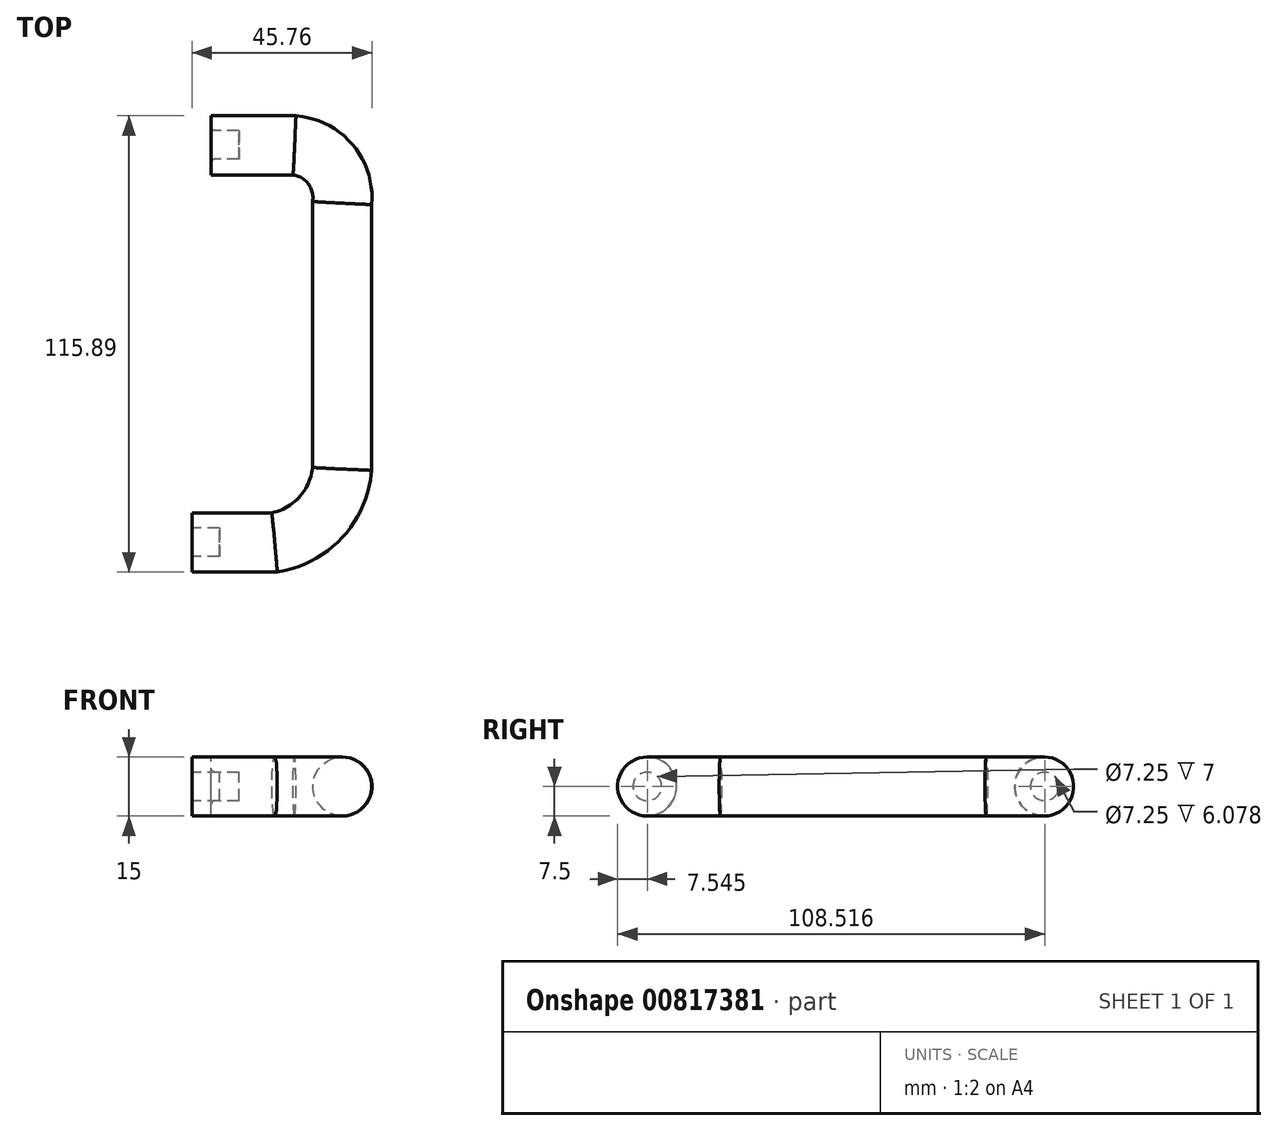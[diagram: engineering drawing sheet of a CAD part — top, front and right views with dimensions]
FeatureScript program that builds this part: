
annotation { "Feature Type Name" : "Feature", "Feature Type Description" : "" }
export const myFeature = defineFeature(function(context is Context, id is Id, definition is map)
    precondition{}
    {
        {
            var Q0;
            Q0=qCreatedBy(makeId("Right.planeOp"),FACE);
            cPlane(context, id + "F0", {"entities" : qUnion([Q0]), "cplaneType" : CPlaneType.OFFSET, "offset" : 5 * mm, "width" : 150 * mm, "height" : 150 * mm});
        }
        {
            var Q0;
            Q0=qCreatedBy(id+"F0.planeOp",FACE);
            var sketch = newSketch(context, id + "F1", { "sketchPlane" : qUnion([Q0])});
            skCircle(sketch, "E0", {"center": v(50.25, 0) * mm, "radius": 7.5 * mm});
            skSolve(sketch);
        }
        {
            var Q0;
            Q0=qCreatedBy(makeId("Top.planeOp"),FACE);
            var sketch = newSketch(context, id + "F2", { "sketchPlane" : qUnion([Q0])});
            skLineSegment(sketch, "E1", {"start": v(0, -50.66) * mm, "end": v(21.06, -50.66) * mm});
            skLineSegment(sketch, "E2", {"start": v(38.2, -32) * mm, "end": v(38.2, 35.56) * mm});
            skLineSegment(sketch, "E3", {"start": v(26.12, 50.27) * mm, "end": v(4.92, 50.27) * mm});
            skArc(sketch, "E4", {"start": v(38.2, 35.56) * mm, "mid": v(35.25, 45.46) * mm, "end": v(26.12, 50.27) * mm});
            skArc(sketch, "E5", {"start": v(21.06, -50.66) * mm, "mid": v(32.79, -44.23) * mm, "end": v(38.2, -32) * mm});
            skSolve(sketch);
        }
        {
            var Q0;
            Q0=makeQuery(id+"F1.imprint","IMPRINT",FACE,{"disambiguationData":[TD([[makeQuery(id+"F1.imprint","IMPRINT",EDGE,{"derivedFrom":sQuery(id+"F1.wireOp",EDGE,"E0")}),1.0]])]});
            var Q1;
            Q1=sQuery(id+"F2.wireOp",EDGE,"E3");
            var Q2;
            Q2=sQuery(id+"F2.wireOp",EDGE,"E2");
            var Q3;
            Q3=sQuery(id+"F2.wireOp",EDGE,"E1");
            var Q4;
            Q4=sQuery(id+"F2.wireOp",EDGE,"E4");
            var Q5;
            Q5=sQuery(id+"F2.wireOp",EDGE,"E5");
            sweep(context, id + "F3", {"profiles" : qUnion([Q0]), "path" : qUnion([Q1, Q2, Q3, Q4, Q5])});
        }
        {
            var Q0;
            Q0=qCreatedBy(makeId("Right.planeOp"),FACE);
            var sketch = newSketch(context, id + "F4", { "sketchPlane" : qUnion([Q0])});
            skCircle(sketch, "E6", {"center": v(-50.6, 0) * mm, "radius": 3.62 * mm});
            skSolve(sketch);
        }
        {
            var Q0;
            Q0=qCreatedBy(id+"F0.planeOp",FACE);
            var sketch = newSketch(context, id + "F5", { "sketchPlane" : qUnion([Q0])});
            skCircle(sketch, "E7", {"center": v(50.38, 0) * mm, "radius": 3.62 * mm});
            skSolve(sketch);
        }
        {
            var Q0;
            Q0=makeQuery(id+"F4.imprint","IMPRINT",FACE,{"disambiguationData":[TD([[makeQuery(id+"F4.imprint","IMPRINT",EDGE,{"derivedFrom":sQuery(id+"F4.wireOp",EDGE,"E6")}),1.0]])]});
            extrude(context, id + "F6", {"entities" : qUnion([Q0]), "operationType" : NewBodyOperationType.REMOVE, "depth" : 7 * mm, "offsetDistance" : 25 * mm});
        }
        {
            var Q0;
            Q0 = qSketchRegion(id + "F5", true);
            extrude(context, id + "F7", {"entities" : qUnion([Q0]), "operationType" : NewBodyOperationType.REMOVE, "depth" : 7 * mm, "offsetDistance" : 25 * mm, "hasSecondDirection" : true, "secondDirectionOppositeDirection" : true, "secondDirectionDepth" : 25 * mm});
        }
        {
            var Q0;
            Q0=makeQuery(id+"F6.boolean.opBoolean","COPY",EDGE,{"derivedFrom":makeQuery(id+"F6.opExtrude","CAP_EDGE",EDGE,{"disambiguationData":[OSD([sQuery(id+"F4.wireOp",EDGE,"E6")])],"isStart":true})});
            var Q1;
            Q1=makeQuery(id+"F7.boolean.opBoolean","INTERSECT",EDGE,{"derivedFrom":[makeQuery(id+"F3.opSweep","CAP_FACE",FACE,{"disambiguationData":[OSD([sQuery(id+"F1.wireOp",EDGE,"E0"),sQuery(id+"F2.wireOp",VERTEX,"E3.end")])],"isStart":true}),makeQuery(id+"F7.opExtrude","SWEPT_FACE",FACE,{"disambiguationData":[OSD([sQuery(id+"F5.wireOp",EDGE,"E7")])]})]});
            fillet(context, id + "F8", {"entities" : qUnion([Q0, Q1]), "radius" : 1 * mm, "tangentPropagation" : true, "allowEdgeOverflow" : false});
        }
    });
